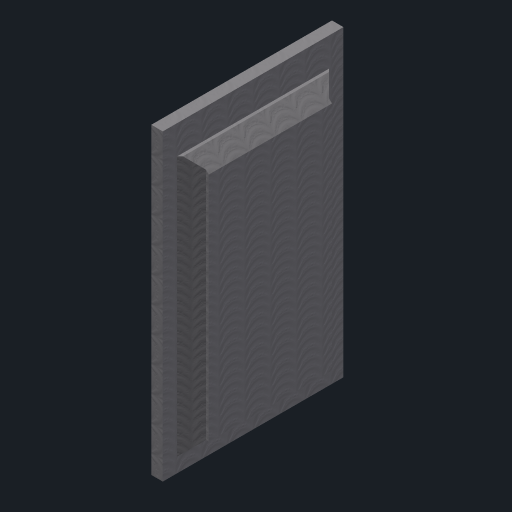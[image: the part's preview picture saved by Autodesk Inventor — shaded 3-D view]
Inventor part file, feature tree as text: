
AUTODESK INVENTOR PART (.ipt)
format: ipt  version: 2024.3 (Build 283343000, 343)  size: 194,048 bytes
history: native  units: mm
features: extrude x3, sketch x2, chamfer x1, projected_geometry x1
ambient origin geometry x8: Origin, YZ Plane, XZ Plane, XY Plane, X Axis, Y Axis, Z Axis, Center Point
bodies: Solid1 (feature_tree)
feature tree (7):
  sketch  "Sketch1"  dims[d0=487.0mm d1=274.0mm]
  extrude  "Extrusion1"  Depth=274.0mm
  extrude  "Extrusion2"  Depth=20.0mm TaperAngle=0.0deg
  extrude  "Extrusion3"  Depth=2.0mm TaperAngle=0.0deg
  chamfer  "Chamfer1"  Distance=50.0mm
  sketch  "Sketch2"  dims[d2=20.0mm d3=20.0mm d4=0.0mm d5=2.0mm d6=0.0mm d7=50.0mm d8=30.0mm d9=0.0mm d10=25.0mm d11=2.0mm d12=45.0deg]
  projected_geometry  "Projected Loop1"
